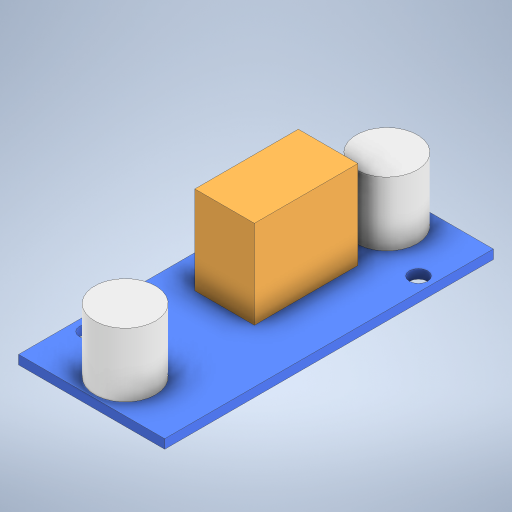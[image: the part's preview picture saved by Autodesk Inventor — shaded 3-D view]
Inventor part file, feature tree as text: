
AUTODESK INVENTOR PART (.ipt)
format: ipt  version: 2023 (Build 270158000, 158)  size: 292,864 bytes
history: native  units: mm
features: extrude x3, sketch x3, other x1
ambient origin geometry x8: Origin, YZ Plane, XZ Plane, XY Plane, X Axis, Y Axis, Z Axis, Center Point
bodies: Body1 (feature_tree)
feature tree (7):
  other  "솔리드1"
  extrude  "돌출1"  Depth=24.0mm
  extrude  "돌출2"  Depth=54.0mm
  extrude  "돌출3"  Depth=3.0mm
  sketch  "스케치1"
  sketch  "스케치2"
  sketch  "스케치3"
